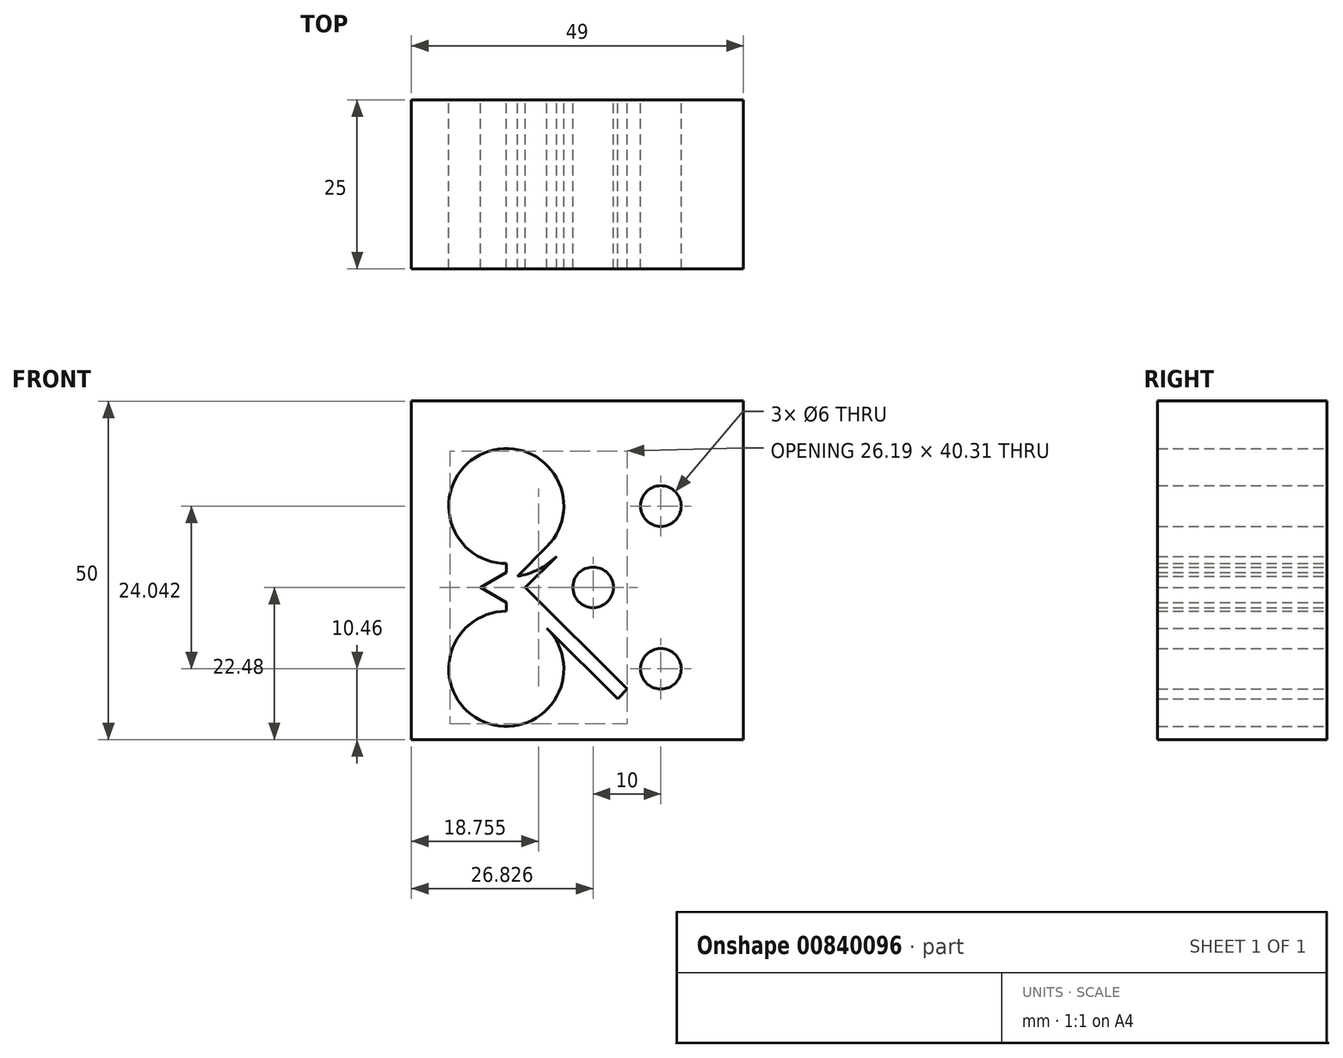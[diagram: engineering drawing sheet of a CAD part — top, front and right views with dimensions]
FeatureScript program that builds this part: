
annotation { "Feature Type Name" : "Feature", "Feature Type Description" : "" }
export const myFeature = defineFeature(function(context is Context, id is Id, definition is map)
    precondition{}
    {
        {
            var Q0;
            Q0=qCreatedBy(makeId("Front.planeOp"),FACE);
            var sketch = newSketch(context, id + "F0", { "sketchPlane" : qUnion([Q0])});
            skArc(sketch, "E0", {"start": v(-38.06, 19.14) * mm, "mid": v(-35.97, 27.7) * mm, "end": v(-42.6, 33.52) * mm});
            skLineSegment(sketch, "E1", {"start": v(-38.06, 19.14) * mm, "end": v(-40.55, 16.65) * mm});
            skLineSegment(sketch, "E2", {"start": v(-44.07, 13.13) * mm, "end": v(-29.32, -1.62) * mm});
            skLineSegment(sketch, "E3", {"start": v(-40.55, 16.65) * mm, "end": v(-44.07, 13.13) * mm});
            skPoint(sketch, "E4", {"position": v(-44.07, 1.1) * mm});
            skLineSegment(sketch, "E5", {"start": v(-41.24, 13.13) * mm, "end": v(-36.65, 17.73) * mm});
            skLineSegment(sketch, "E6", {"start": v(-41.24, 13.13) * mm, "end": v(-26.22, -1.9) * mm});
            skLineSegment(sketch, "E7", {"start": v(-29.32, -1.62) * mm, "end": v(-27.64, -3.3) * mm});
            skLineSegment(sketch, "E8", {"start": v(-26.22, -1.9) * mm, "end": v(-27.64, -3.3) * mm});
            skPoint(sketch, "E9", {"position": v(-42.11, -0.85) * mm});
            skPoint(sketch, "E10.orphan", {"position": v(-44.07, -0.85) * mm});
            skPoint(sketch, "E11.bottom.end.orphan", {"position": v(-35.57, -0.85) * mm});
            skPoint(sketch, "E12.end.orphan", {"position": v(-30.1, -0.85) * mm});
            skPoint(sketch, "E12.start.orphan", {"position": v(-32.05, -0.85) * mm});
            skCircle(sketch, "E13", {"center": v(-44.07, 1.1) * mm, "radius": 8.5 * mm});
            skLineSegment(sketch, "E14", {"start": v(-44.07, 25.15) * mm, "end": v(-39.22, 20.3) * mm});
            skPoint(sketch, "E15.orphan", {"position": v(-42.25, 35.5) * mm});
            skArc(sketch, "E16", {"start": v(-36.65, 17.73) * mm, "mid": v(-34.06, 28.3) * mm, "end": v(-42.25, 35.5) * mm});
            skLineSegment(sketch, "E17", {"start": v(-26.22, -1.9) * mm, "end": v(-18.76, -9.35) * mm});
            skCircle(sketch, "E18", {"center": v(-44.07, 25.15) * mm, "radius": 8.5 * mm});
            skLineSegment(sketch, "E19", {"start": v(-44.07, 25.15) * mm, "end": v(-44.07, 1.1) * mm});
            skLineSegment(sketch, "E20", {"start": v(-44.07, 25.15) * mm, "end": v(-44.07, 35.65) * mm});
            skArc(sketch, "E21", {"start": v(-44.07, 14.65) * mm, "mid": v(-33.57, 25.15) * mm, "end": v(-44.07, 35.65) * mm});
            skLineSegment(sketch, "E22", {"start": v(-27.64, -3.3) * mm, "end": v(-19.46, -11.49) * mm});
            skPoint(sketch, "E23", {"position": v(-44.07, 40.65) * mm});
            skLineSegment(sketch, "E24", {"start": v(-44.07, 40.65) * mm, "end": v(-9.07, 40.65) * mm});
            skLineSegment(sketch, "E25", {"start": v(-9.07, 40.65) * mm, "end": v(-9.07, -9.35) * mm});
            skLineSegment(sketch, "E26", {"start": v(-9.07, -9.35) * mm, "end": v(-18.76, -9.35) * mm});
            skLineSegment(sketch, "E27", {"start": v(-36.65, 17.73) * mm, "end": v(-18.76, 35.6) * mm});
            skPoint(sketch, "E28", {"position": v(-31.24, 13.13) * mm});
            skPoint(sketch, "E29", {"position": v(-16.24, 1.1) * mm});
            skPoint(sketch, "E30.positionSnap0", {"position": v(-33.57, 25.15) * mm});
            skCircle(sketch, "E31", {"center": v(-31.24, 13.13) * mm, "radius": 3 * mm});
            skLineSegment(sketch, "E32", {"start": v(-18.76, 35.6) * mm, "end": v(-9.07, 35.6) * mm});
            skLineSegment(sketch, "E33", {"start": v(-44.07, 40.65) * mm, "end": v(-44.07, 35.65) * mm});
            skLineSegment(sketch, "E34", {"start": v(-44.07, 40.65) * mm, "end": v(-58.07, 40.65) * mm});
            skLineSegment(sketch, "E35.bottom", {"start": v(-18.76, -9.35) * mm, "end": v(-58.07, -9.35) * mm});
            skLineSegment(sketch, "E35.top", {"start": v(-18.76, 40.65) * mm, "end": v(-58.07, 40.65) * mm});
            skLineSegment(sketch, "E35.right", {"start": v(-58.07, -9.35) * mm, "end": v(-58.07, 40.65) * mm});
            skPoint(sketch, "E36", {"position": v(-21.24, 25.15) * mm});
            skPoint(sketch, "E37", {"position": v(-21.24, 1.1) * mm});
            skCircle(sketch, "E38", {"center": v(-21.24, 25.15) * mm, "radius": 3 * mm});
            skCircle(sketch, "E39", {"center": v(-21.24, 1.1) * mm, "radius": 3 * mm});
            skPoint(sketch, "E40", {"position": v(-58.07, 37.24) * mm});
            skLineSegment(sketch, "E41", {"start": v(-39.82, 17.8) * mm, "end": v(-58.07, 7.25) * mm});
            skLineSegment(sketch, "E42", {"start": v(-39.82, 8.47) * mm, "end": v(-59.06, 19.58) * mm});
            skLineSegment(sketch, "E43", {"start": v(-59.06, 19.58) * mm, "end": v(-92.66, 35.76) * mm});
            skSolve(sketch);
        }
        {
            var Q0;
            {var subQ8=sQuery(id+"F0.wireOp",EDGE,"E1");Q0=makeQuery(id+"F0.imprint","IMPRINT",FACE,{"disambiguationData":[TD([[makeQuery(id+"F0.imprint","IMPRINT",EDGE,{"derivedFrom":subQ8}),1.0]])]});}
            extrude(context, id + "F1", {"entities" : qUnion([Q0]), "depth" : 25 * mm, "offsetDistance" : 25 * mm});
        }
        {
            var Q0;
            Q0=qSketchRegion(id+"F0",true);
            extrude(context, id + "F2", {"entities" : qUnion([Q0]), "operationType" : NewBodyOperationType.ADD, "depth" : 25 * mm, "offsetDistance" : 25 * mm});
        }
    });
